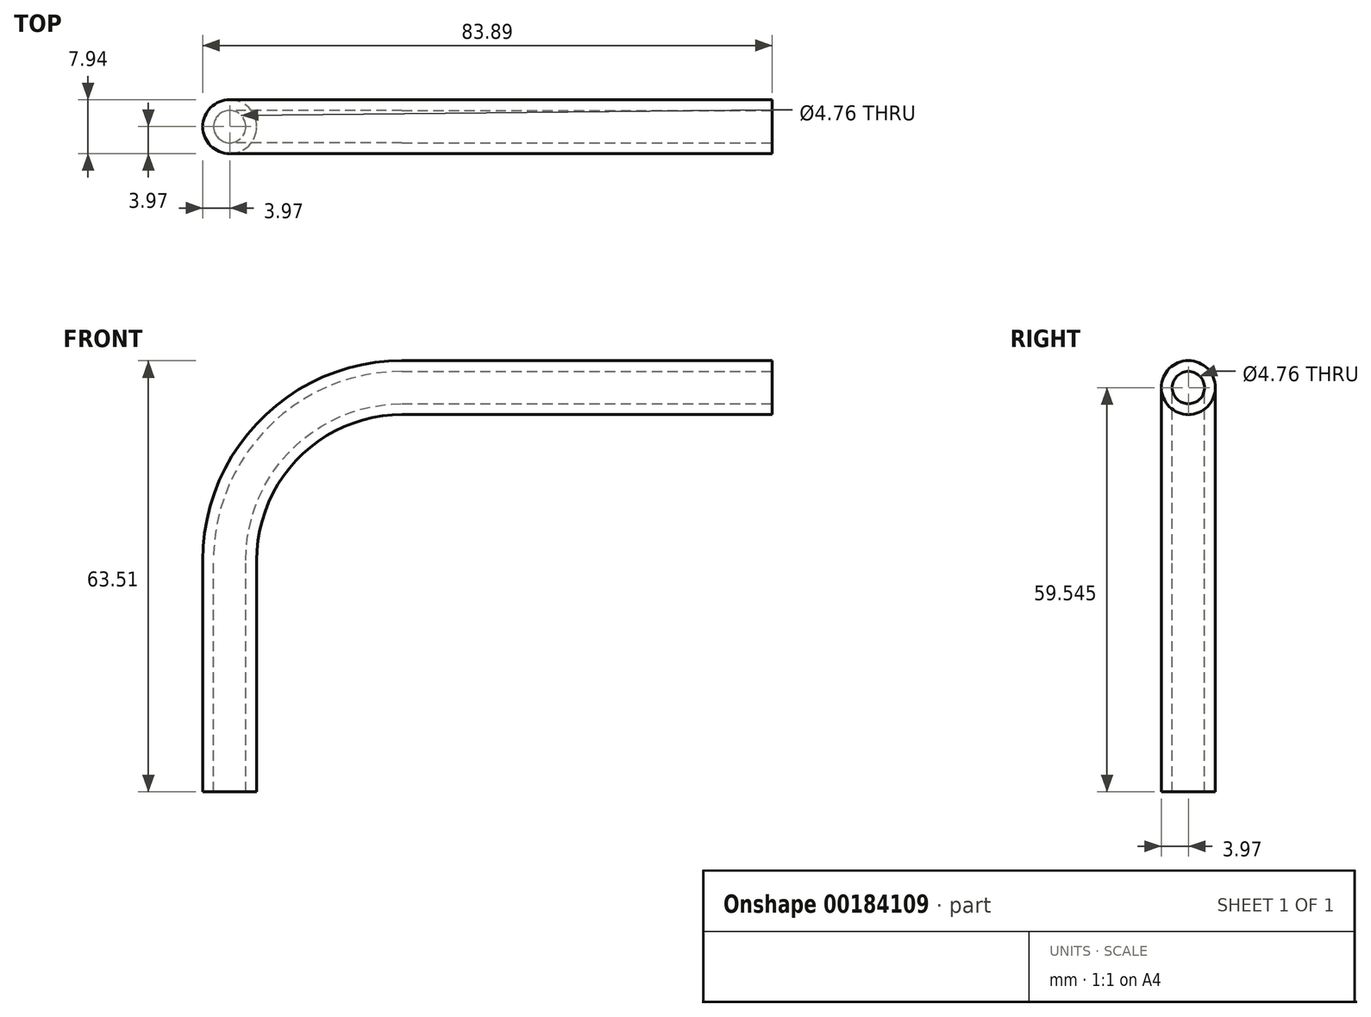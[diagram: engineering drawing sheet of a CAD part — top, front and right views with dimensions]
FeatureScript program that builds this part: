
annotation { "Feature Type Name" : "Feature", "Feature Type Description" : "" }
export const myFeature = defineFeature(function(context is Context, id is Id, definition is map)
    precondition{}
    {
        {
            var Q0;
            Q0=qCreatedBy(makeId("Front.planeOp"),FACE);
            var sketch = newSketch(context, id + "F0", { "sketchPlane" : qUnion([Q0])});
            skLineSegment(sketch, "E0", {"start": v(0, 0) * mm, "end": v(0, 34.15) * mm});
            skLineSegment(sketch, "E1", {"start": v(25.4, 59.55) * mm, "end": v(79.92, 59.55) * mm});
            skPoint(sketch, "E2.visualSharp", {"position": v(0, 59.55) * mm});
            skArc(sketch, "E2.filletArc", {"start": v(25.4, 59.55) * mm, "mid": v(7.44, 52.1) * mm, "end": v(0, 34.15) * mm});
            skSolve(sketch);
        }
        {
            var Q0;
            Q0=qCreatedBy(makeId("Top.planeOp"),FACE);
            var sketch = newSketch(context, id + "F1", { "sketchPlane" : qUnion([Q0])});
            skCircle(sketch, "E3", {"center": v(0, 0) * mm, "radius": 3.97 * mm});
            skCircle(sketch, "E4", {"center": v(0, 0) * mm, "radius": 2.38 * mm});
            skSolve(sketch);
        }
        {
            var Q0;
            Q0=makeQuery(id+"F1.imprint","IMPRINT",FACE,{"disambiguationData":[TD([[makeQuery(id+"F1.imprint","IMPRINT",EDGE,{"derivedFrom":sQuery(id+"F1.wireOp",EDGE,"E3")}),1.0]])]});
            var Q1;
            Q1 = qConstructionFilter(qBodyType(qCreatedBy(id + "F0" ,EDGE), BodyType.WIRE), ConstructionObject.NO);
            sweep(context, id + "F2", {"profiles" : qUnion([Q0]), "path" : qUnion([Q1])});
        }
    });
